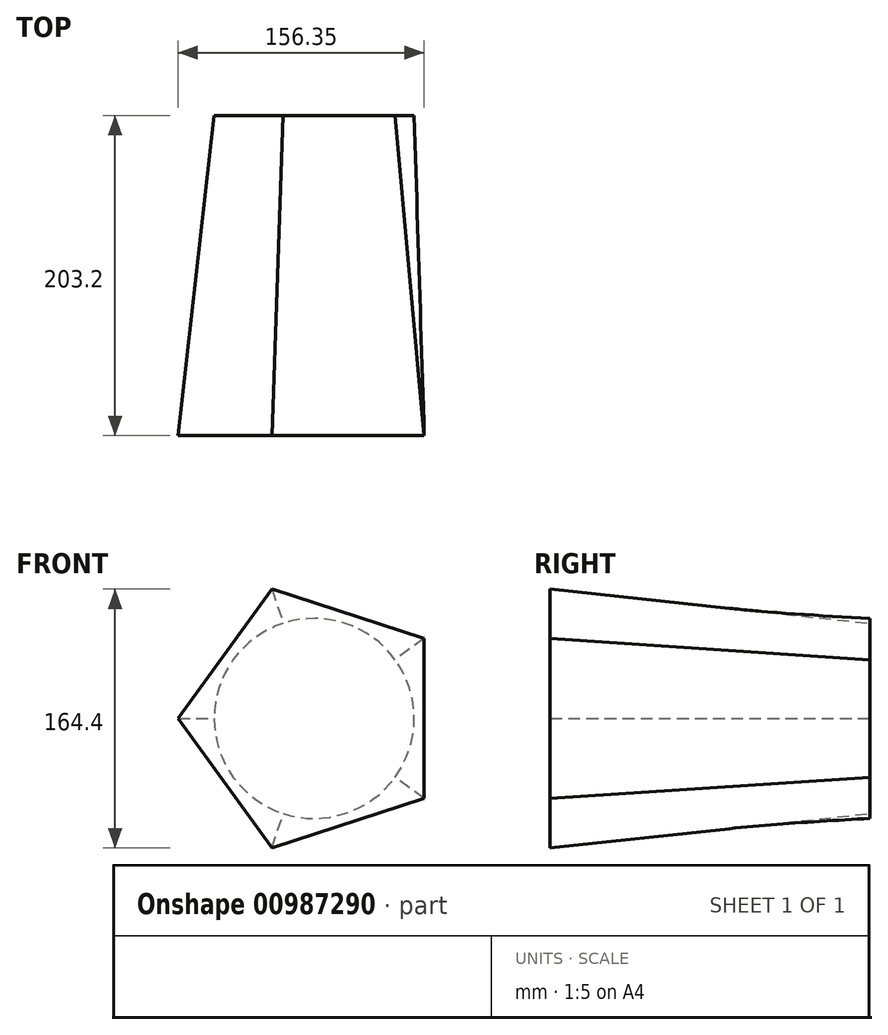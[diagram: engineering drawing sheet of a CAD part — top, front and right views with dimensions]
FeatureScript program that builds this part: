
annotation { "Feature Type Name" : "Feature", "Feature Type Description" : "" }
export const myFeature = defineFeature(function(context is Context, id is Id, definition is map)
    precondition{}
    {
        {
            var Q0;
            Q0=qCreatedBy(makeId("Front.planeOp"),FACE);
            var sketch = newSketch(context, id + "F0", { "sketchPlane" : qUnion([Q0])});
            skCircle(sketch, "E0", {"center": v(0, 0) * mm, "radius": 63.5 * mm});
            skSolve(sketch);
        }
        {
            var Q0;
            Q0=makeQuery(id+"F0.imprint","IMPRINT",FACE,{"disambiguationData":[TD([[makeQuery(id+"F0.imprint","IMPRINT",EDGE,{"derivedFrom":sQuery(id+"F0.wireOp",EDGE,"E0")}),1.0]])]});
            cPlane(context, id + "F1", {"entities" : qUnion([Q0]), "cplaneType" : CPlaneType.OFFSET, "offset" : 203.2 * mm, "width" : 152.4 * mm, "height" : 152.4 * mm});
        }
        {
            var Q0;
            Q0=qCreatedBy(id+"F1.planeOp",FACE);
            var sketch = newSketch(context, id + "F2", { "sketchPlane" : qUnion([Q0])});
            skCircle(sketch, "E1.cCircle", {"center": v(0, 0) * mm, "radius": 69.92 * mm, "construction": true});
            skLineSegment(sketch, "E1.0", {"start": v(69.92, 50.8) * mm, "end": v(69.92, -50.8) * mm});
            skLineSegment(sketch, "E1.1", {"start": v(69.92, -50.8) * mm, "end": v(-26.7, -82.2) * mm});
            skLineSegment(sketch, "E1.2", {"start": v(-26.7, -82.2) * mm, "end": v(-86.43, 0) * mm});
            skLineSegment(sketch, "E1.3", {"start": v(-86.43, 0) * mm, "end": v(-26.7, 82.2) * mm});
            skLineSegment(sketch, "E1.4", {"start": v(-26.7, 82.2) * mm, "end": v(69.92, 50.8) * mm});
            skPoint(sketch, "E1.0.midPoint", {"position": v(69.92, 0) * mm});
            skSolve(sketch);
        }
        {
            var Q0;
            Q0=makeQuery(id+"F2.imprint","IMPRINT",FACE,{"disambiguationData":[TD([[makeQuery(id+"F2.imprint","IMPRINT",EDGE,{"derivedFrom":sQuery(id+"F2.wireOp",EDGE,"E1.0")}),-1.0]])]});
            var Q1;
            Q1=makeQuery(id+"F0.imprint","IMPRINT",FACE,{"disambiguationData":[TD([[makeQuery(id+"F0.imprint","IMPRINT",EDGE,{"derivedFrom":sQuery(id+"F0.wireOp",EDGE,"E0")}),1.0]])]});
            loft(context, id + "F3", {"sheetProfilesArray" : [{ "sheetProfileEntities" : qUnion([Q0]) }, { "sheetProfileEntities" : qUnion([Q1]) }]});
        }
    });
